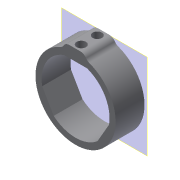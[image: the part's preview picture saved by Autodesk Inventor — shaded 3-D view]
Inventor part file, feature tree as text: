
AUTODESK INVENTOR PART (.ipt)
format: ipt  version: 2019.4 (Build 234330000, 330)  size: 163,328 bytes
history: native  units: mm
features: other x4, extrude x3, reference x3, sketch x2, plane x1, pattern_circular x1, fillet x1, projected_geometry x1
ambient origin geometry x8: Origin, YZ Plane, XZ Plane, XY Plane, X Axis, Y Axis, Z Axis, Center Point
bodies: Solid1 (feature_tree)
feature tree (16):
  plane  "Work Plane2"
  extrude  "Extrusion1"  Depth=9.0mm TaperAngle=0.0deg
  pattern_circular  "Circular Pattern1"  Count=3 Angle=360.0deg
  extrude  "Extrusion2"  Depth=10.0mm TaperAngle=0.0deg
  fillet  "Fillet1"  Radius=2.0mm
  extrude  "Extrusion3"  Depth=10.0mm TaperAngle=0.0deg
  reference  "Reference1"
  reference  "Reference2"
  reference  "Reference3"
  sketch  "Sketch3"  dims[d1=25.0mm d3=9.0mm d4=0.0mm d5=30.0mm d6=360.0deg]
  sketch  "Sketch4"  dims[d9=7.0mm d10=10.0mm d11=0.0mm d12=2.0mm d15=10.0mm d16=0.0mm d17=0.5mm d18=2.9mm d19=2.9mm d20=2.0mm d21=5.0mm]
  projected_geometry  "Projected Loop2"
  other  "Assembly_Opentrons_Autofocus_v1.iam"
  other  "Assembly_Autofocus_10x_laser_espcam_v1:1"
  other  "20_focus_inlet_linearflexure_objective_mount_v0:1"
  other  "00_objectivelens_10x:1"
